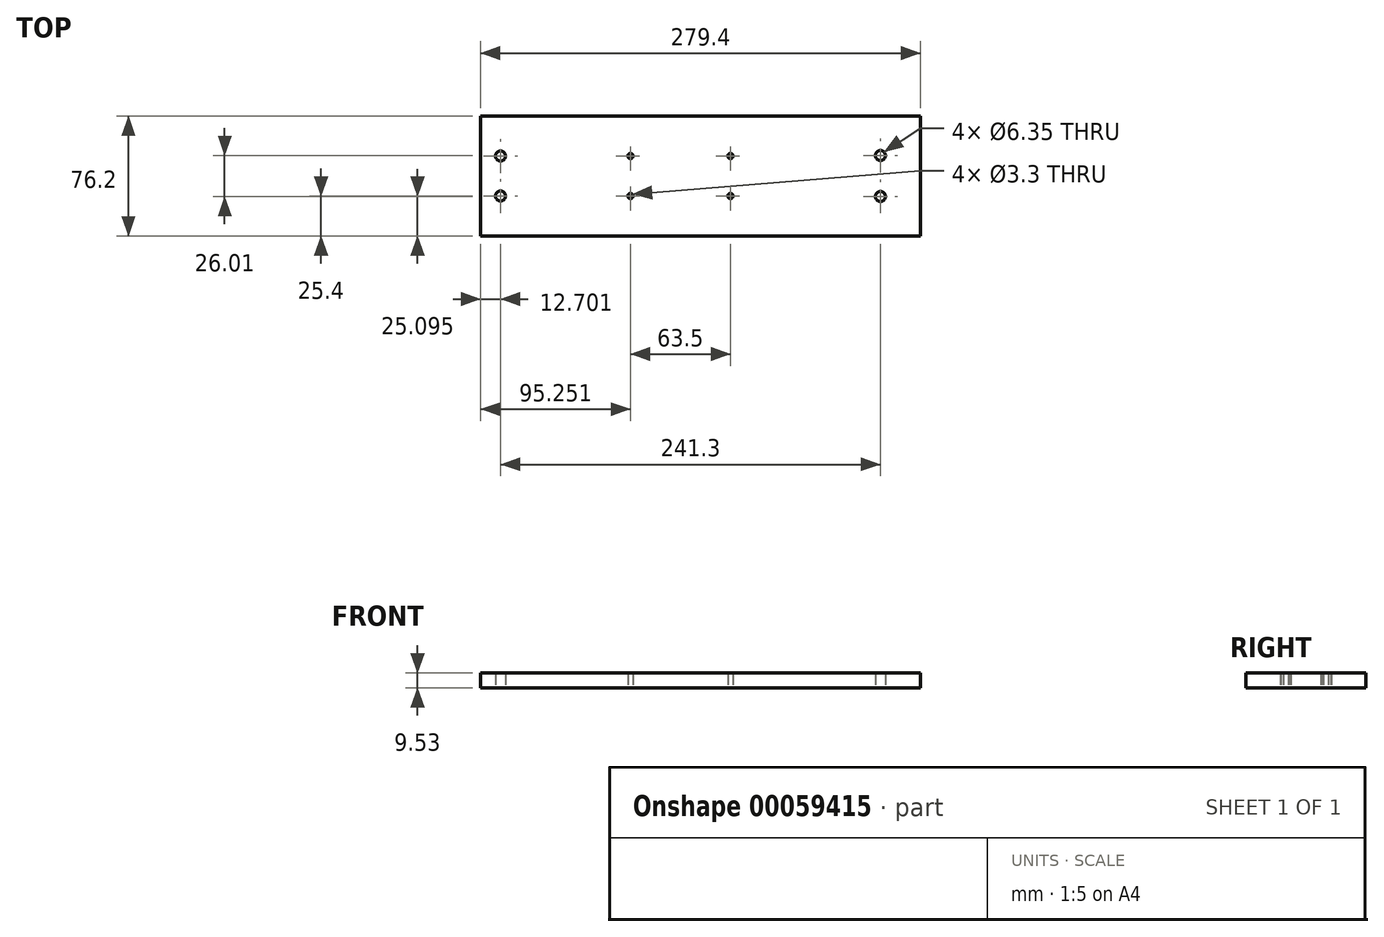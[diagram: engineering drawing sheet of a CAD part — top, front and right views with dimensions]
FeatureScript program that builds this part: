
annotation { "Feature Type Name" : "Feature", "Feature Type Description" : "" }
export const myFeature = defineFeature(function(context is Context, id is Id, definition is map)
    precondition{}
    {
        {
            var Q0;
            Q0=qCreatedBy(makeId("Top.planeOp"),FACE);
            var sketch = newSketch(context, id + "F0", { "sketchPlane" : qUnion([Q0])});
            skLineSegment(sketch, "E0.bottom", {"start": v(-135.9, 38.34) * mm, "end": v(143.5, 38.34) * mm});
            skLineSegment(sketch, "E0.top", {"start": v(-135.9, -37.86) * mm, "end": v(143.5, -37.86) * mm});
            skLineSegment(sketch, "E0.left", {"start": v(-135.9, 38.34) * mm, "end": v(-135.9, -37.86) * mm});
            skLineSegment(sketch, "E0.right", {"start": v(143.5, 38.34) * mm, "end": v(143.5, -37.86) * mm});
            skLineSegment(sketch, "E1", {"start": v(-144.21, 0.24) * mm, "end": v(173.95, 0.24) * mm, "construction": true});
            skLineSegment(sketch, "E2", {"start": v(-130.21, 12.94) * mm, "end": v(165.55, 12.94) * mm, "construction": true});
            skLineSegment(sketch, "E3", {"start": v(-131.96, -12.46) * mm, "end": v(167.3, -12.46) * mm, "construction": true});
            skCircle(sketch, "E4", {"center": v(-123.2, 12.94) * mm, "radius": 3.18 * mm});
            skCircle(sketch, "E5", {"center": v(-123.2, -12.46) * mm, "radius": 3.18 * mm});
            skCircle(sketch, "E6", {"center": v(-40.65, 12.94) * mm, "radius": 1.65 * mm});
            skCircle(sketch, "E7", {"center": v(-40.65, -12.46) * mm, "radius": 1.65 * mm});
            skCircle(sketch, "E8", {"center": v(22.85, 12.94) * mm, "radius": 1.65 * mm});
            skCircle(sketch, "E9", {"center": v(22.85, -12.46) * mm, "radius": 1.65 * mm});
            skCircle(sketch, "E10", {"center": v(118.1, 13.24) * mm, "radius": 3.18 * mm});
            skCircle(sketch, "E11", {"center": v(118.1, -12.76) * mm, "radius": 3.18 * mm});
            skSolve(sketch);
        }
        {
            var Q0;
            Q0 = qSketchRegion(id + "F0", true);
            extrude(context, id + "F1", {"entities" : qUnion([Q0]), "depth" : 9.52 * mm});
        }
    });
